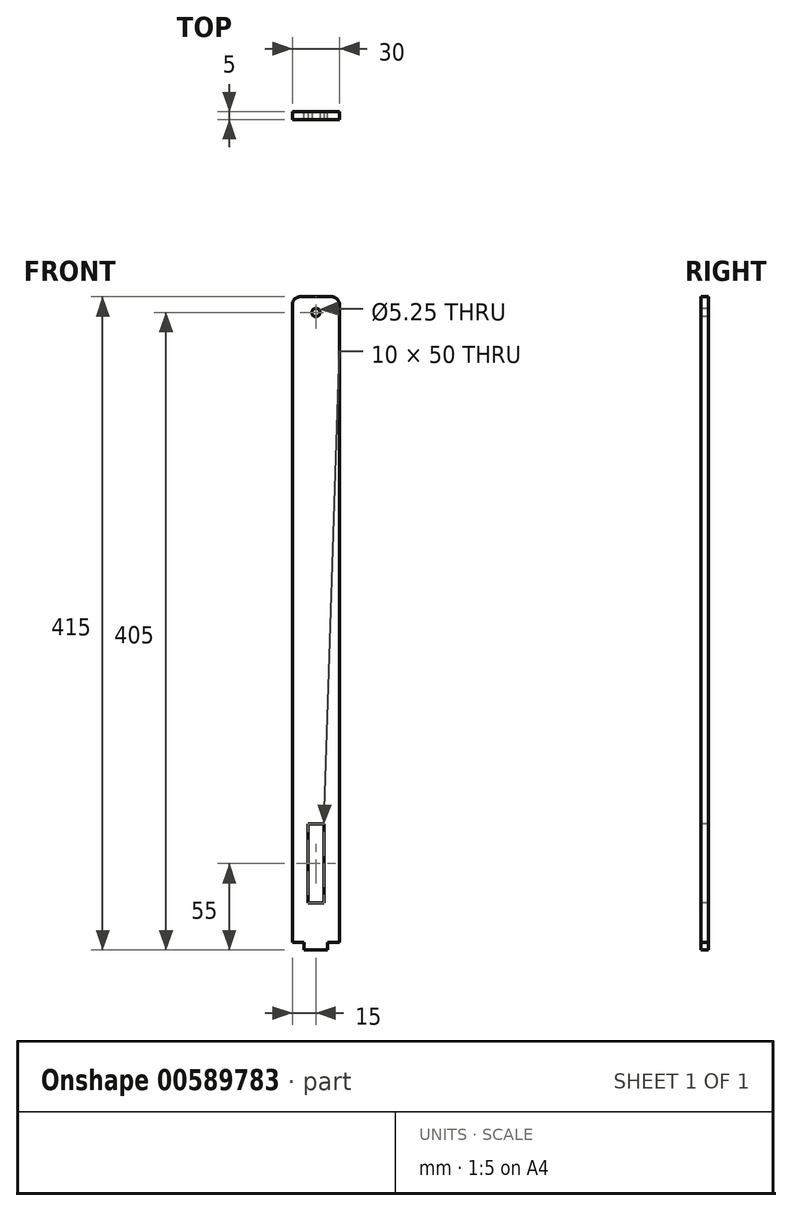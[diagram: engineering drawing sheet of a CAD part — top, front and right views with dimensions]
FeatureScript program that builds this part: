
annotation { "Feature Type Name" : "Feature", "Feature Type Description" : "" }
export const myFeature = defineFeature(function(context is Context, id is Id, definition is map)
    precondition{}
    {
        {
            var Q0;
            Q0=qCreatedBy(makeId("Front.planeOp"),FACE);
            var sketch = newSketch(context, id + "F0", { "sketchPlane" : qUnion([Q0])});
            skLineSegment(sketch, "E0.bottom", {"start": v(15, 205) * mm, "end": v(-15, 205) * mm});
            skLineSegment(sketch, "E0.top", {"start": v(15, -205) * mm, "end": v(-15, -205) * mm});
            skLineSegment(sketch, "E0.left", {"start": v(15, 205) * mm, "end": v(15, -205) * mm});
            skLineSegment(sketch, "E0.right", {"start": v(-15, 205) * mm, "end": v(-15, -205) * mm});
            skPoint(sketch, "E0.middle", {"position": v(0, 0) * mm});
            skLineSegment(sketch, "E1.bottom", {"start": v(7.5, -210) * mm, "end": v(-7.5, -210) * mm});
            skLineSegment(sketch, "E1.top", {"start": v(7.5, -200) * mm, "end": v(-7.5, -200) * mm});
            skLineSegment(sketch, "E1.left", {"start": v(7.5, -210) * mm, "end": v(7.5, -200) * mm});
            skLineSegment(sketch, "E1.right", {"start": v(-7.5, -210) * mm, "end": v(-7.5, -200) * mm});
            skPoint(sketch, "E1.middle", {"position": v(0, -205) * mm});
            skSolve(sketch);
        }
        {
            var Q0;
            Q0=makeQuery(id+"F0.imprint","IMPRINT",FACE,{"disambiguationData":[TD([[makeQuery(id+"F0.imprint","IMPRINT",EDGE,{"derivedFrom":sQuery(id+"F0.wireOp",EDGE,"E0.bottom")}),1.0]])]});
            var Q1;
            {var subQ5=sQuery(id+"F0.wireOp",EDGE,"E1.bottom");Q1=makeQuery(id+"F0.imprint","IMPRINT",FACE,{"disambiguationData":[TD([[makeQuery(id+"F0.imprint","IMPRINT",EDGE,{"derivedFrom":subQ5}),-1.0]])]});}
            var Q2;
            {var subQ5=sQuery(id+"F0.wireOp",EDGE,"E1.top");Q2=makeQuery(id+"F0.imprint","IMPRINT",FACE,{"disambiguationData":[TD([[makeQuery(id+"F0.imprint","IMPRINT",EDGE,{"derivedFrom":subQ5}),1.0]])]});}
            extrude(context, id + "F1", {"entities" : qUnion([Q0, Q1, Q2]), "endBound" : BoundingType.SYMMETRIC, "depth" : 5 * mm, "offsetDistance" : 25 * mm});
        }
        {
            var Q0;
            Q0=makeQuery(id+"F1.opExtrude","CAP_FACE",FACE,{"disambiguationData":[OSD([sQuery(id+"F0.wireOp",EDGE,"E0.bottom"),sQuery(id+"F0.wireOp",EDGE,"E0.top"),sQuery(id+"F0.wireOp",EDGE,"E0.left"),sQuery(id+"F0.wireOp",EDGE,"E0.right"),sQuery(id+"F0.wireOp",EDGE,"E1.bottom"),sQuery(id+"F0.wireOp",EDGE,"E1.left"),sQuery(id+"F0.wireOp",EDGE,"E1.right")])],"isStart":false});
            var sketch = newSketch(context, id + "F2", { "sketchPlane" : qUnion([Q0])});
            skPoint(sketch, "E2", {"position": v(0, 195) * mm});
            skSolve(sketch);
        }
        {
            var Q0;
            Q0=sQuery(id+"F2.wireOp",VERTEX,"E2");
            var Q1;
            Q1=makeQuery(id+"F1.opExtrude","SWEPT_BODY",BODY,{"disambiguationData":[OSD([sQuery(id+"F0.wireOp",EDGE,"E0.bottom"),sQuery(id+"F0.wireOp",EDGE,"E0.top"),sQuery(id+"F0.wireOp",EDGE,"E0.left"),sQuery(id+"F0.wireOp",EDGE,"E0.right"),sQuery(id+"F0.wireOp",EDGE,"E1.bottom"),sQuery(id+"F0.wireOp",EDGE,"E1.left"),sQuery(id+"F0.wireOp",EDGE,"E1.right")])]});
            hole(context, id + "F3", {"style" : HoleStyle.SIMPLE, "endStyle" : HoleEndStyle.THROUGH, "standardTappedOrClearance" : lookupTablePath({ "standard" : "ISO", "fit" : "Close", "size" : "M5", "type" : "Clearance" }), "standardBlindInLast" : lookupTablePath({ "fit" : "Close", "standard" : "ISO", "size" : "M5", "type" : "Clearance" }), "holeDiameter" : 5.25 * mm, "majorDiameter" : 5 * mm, "isTappedThrough" : true, "tappedDepth" : 12 * mm, "tapClearance" : 3, "locations" : qUnion([Q0]), "scope" : qUnion([Q1])});
        }
        {
            var Q0;
            Q0=makeQuery(id+"F1.opExtrude","SWEPT_EDGE",EDGE,{"disambiguationData":[OSD([sQuery(id+"F0.wireOp",EDGE,"E0.bottom"),sQuery(id+"F0.wireOp",EDGE,"E0.left")])]});
            var Q1;
            Q1=makeQuery(id+"F1.opExtrude","SWEPT_EDGE",EDGE,{"disambiguationData":[OSD([sQuery(id+"F0.wireOp",EDGE,"E0.bottom"),sQuery(id+"F0.wireOp",EDGE,"E0.right")])]});
            fillet(context, id + "F4", {"entities" : qUnion([Q0, Q1]), "radius" : 5 * mm, "tangentPropagation" : true, "allowEdgeOverflow" : false});
        }
        {
            var Q0;
            Q0=makeQuery(id+"F1.opExtrude","CAP_FACE",FACE,{"disambiguationData":[OSD([sQuery(id+"F0.wireOp",EDGE,"E0.bottom"),sQuery(id+"F0.wireOp",EDGE,"E0.top"),sQuery(id+"F0.wireOp",EDGE,"E0.left"),sQuery(id+"F0.wireOp",EDGE,"E0.right"),sQuery(id+"F0.wireOp",EDGE,"E1.bottom"),sQuery(id+"F0.wireOp",EDGE,"E1.left"),sQuery(id+"F0.wireOp",EDGE,"E1.right")])],"isStart":false});
            var sketch = newSketch(context, id + "F5", { "sketchPlane" : qUnion([Q0])});
            skLineSegment(sketch, "E3.bottom", {"start": v(5, -180) * mm, "end": v(-5, -180) * mm});
            skLineSegment(sketch, "E3.top", {"start": v(5, -130) * mm, "end": v(-5, -130) * mm});
            skLineSegment(sketch, "E3.left", {"start": v(5, -180) * mm, "end": v(5, -130) * mm});
            skLineSegment(sketch, "E3.right", {"start": v(-5, -180) * mm, "end": v(-5, -130) * mm});
            skPoint(sketch, "E3.middle", {"position": v(0, -155) * mm});
            skSolve(sketch);
        }
        {
            var Q0;
            Q0=makeQuery(id+"F5.imprint","IMPRINT",FACE,{"disambiguationData":[TD([[makeQuery(id+"F5.imprint","IMPRINT",EDGE,{"derivedFrom":sQuery(id+"F5.wireOp",EDGE,"E3.bottom")}),-1.0]])]});
            extrude(context, id + "F6", {"entities" : qUnion([Q0]), "operationType" : NewBodyOperationType.REMOVE, "oppositeDirection" : true, "depth" : 10 * mm, "offsetDistance" : 25 * mm});
        }
    });
